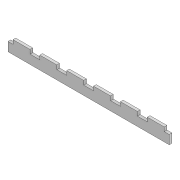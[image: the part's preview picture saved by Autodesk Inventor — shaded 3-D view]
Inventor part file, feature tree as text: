
AUTODESK INVENTOR PART (.ipt)
format: ipt  version: 2022 (Build 260153000, 153)  size: 106,496 bytes
history: native  units: mm
features: extrude x1, sketch x1
ambient origin geometry x8: Origin, YZ Plane, XZ Plane, XY Plane, X Axis, Y Axis, Z Axis, Center Point
bodies: Solid1 (feature_tree)
feature tree (2):
  extrude  "Extrusion1"  Depth=10.0mm
  sketch  "Sketch1"  dims[d0=180.0mm d1=10.0mm d2=19.0mm d3=4.5mm d4=5.5mm d5=60.0mm d7=30.0mm d8=10.0mm d10=10.0mm d12=3.0mm d13=0.0mm]
